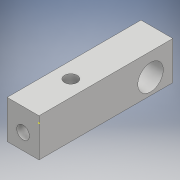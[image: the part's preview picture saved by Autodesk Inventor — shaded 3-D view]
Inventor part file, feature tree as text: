
AUTODESK INVENTOR PART (.ipt)
format: ipt  version: 2017 SP1 (Build 210196100, 196)  size: 134,656 bytes
history: native  units: mm
features: sketch x7, extrude x3, hole x3
ambient origin geometry x8: Origin, YZ Plane, XZ Plane, XY Plane, X Axis, Y Axis, Z Axis, Center Point
bodies: Solide1 (feature_tree)
feature tree (13):
  extrude  "Extrusion1"  Depth=40.0mm
  hole  "Perçage1"  [1 undecoded]
  extrude  "Extrusion2"  Depth=10.0mm TaperAngle=0.0deg
  extrude  "Extrusion3"  Depth=5.0mm
  sketch  "Esquisse5"
  hole  "Perçage2"  [1 undecoded]
  hole  "Perçage3"  [1 undecoded]
  sketch  "Esquisse1"
  sketch  "Esquisse2"
  sketch  "Esquisse3"
  sketch  "Esquisse4"
  sketch  "Esquisse6"
  sketch  "Esquisse7"
note: 3 required parameter values undecoded (feature->parameter linkage not recoverable at this tier; creation-order binding heuristic only, values carry confidence <= 0.55)
